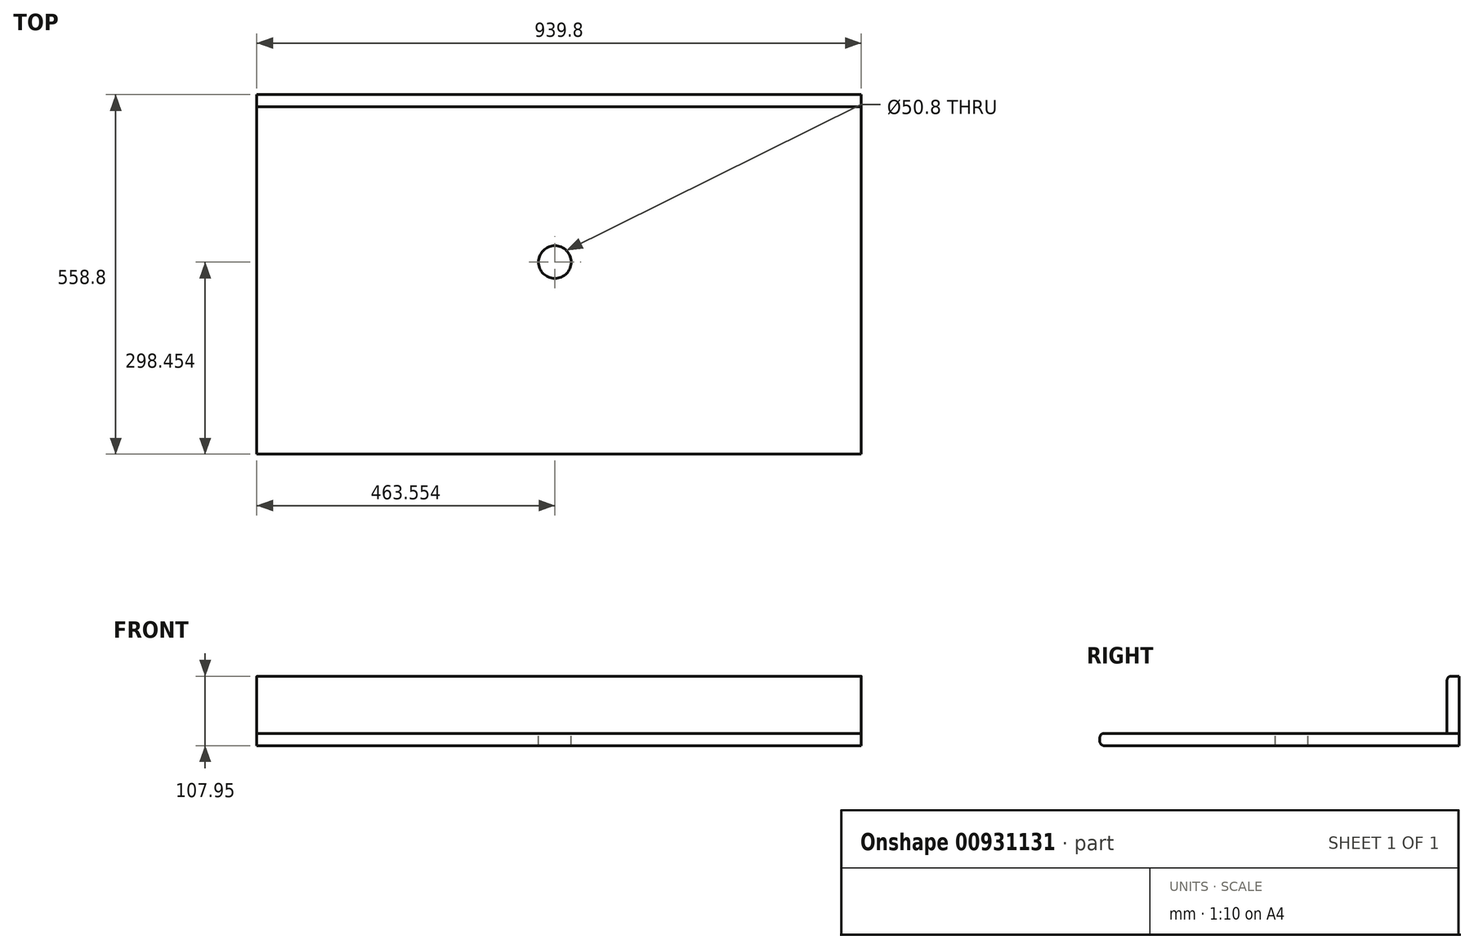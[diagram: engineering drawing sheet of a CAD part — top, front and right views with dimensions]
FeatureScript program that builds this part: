
annotation { "Feature Type Name" : "Feature", "Feature Type Description" : "" }
export const myFeature = defineFeature(function(context is Context, id is Id, definition is map)
    precondition{}
    {
        {
            var Q0;
            Q0=qCreatedBy(makeId("Top.planeOp"),FACE);
            var sketch = newSketch(context, id + "F0", { "sketchPlane" : qUnion([Q0])});
            skLineSegment(sketch, "E0.bottom", {"start": v(-468.4, 352.27) * mm, "end": v(471.4, 352.27) * mm});
            skLineSegment(sketch, "E0.top", {"start": v(-468.4, -206.53) * mm, "end": v(471.4, -206.53) * mm});
            skLineSegment(sketch, "E0.left", {"start": v(-468.4, 352.27) * mm, "end": v(-468.4, -206.53) * mm});
            skLineSegment(sketch, "E0.right", {"start": v(471.4, 352.27) * mm, "end": v(471.4, -206.53) * mm});
            skLineSegment(sketch, "E1.top", {"start": v(-468.4, 333.22) * mm, "end": v(471.4, 333.22) * mm});
            skLineSegment(sketch, "E1.left", {"start": v(-468.4, 352.27) * mm, "end": v(-468.4, 333.22) * mm});
            skLineSegment(sketch, "E1.right", {"start": v(471.4, 352.27) * mm, "end": v(471.4, 333.22) * mm});
            skLineSegment(sketch, "E2", {"start": v(-468.4, 91.92) * mm, "end": v(-4.86, 91.92) * mm});
            skLineSegment(sketch, "E3", {"start": v(-4.86, 91.92) * mm, "end": v(-4.86, -206.53) * mm});
            skCircle(sketch, "E4", {"center": v(-4.86, 91.92) * mm, "radius": 25.4 * mm});
            skSolve(sketch);
        }
        {
            var Q0;
            Q0=makeQuery(id+"F0.imprint","IMPRINT",FACE,{"disambiguationData":[TD([[makeQuery(id+"F0.imprint","IMPRINT",EDGE,{"derivedFrom":sQuery(id+"F0.wireOp",EDGE,"E0.bottom")}),-1.0]])]});
            extrude(context, id + "F1", {"entities" : qUnion([Q0]), "depth" : 88.9 * mm, "offsetDistance" : 25.4 * mm});
        }
        {
            var Q0;
            Q0 = qSketchRegion(id + "F0", true);
            extrude(context, id + "F2", {"entities" : qUnion([Q0]), "depth" : -19.05 * mm, "offsetDistance" : 25.4 * mm});
        }
        {
            var Q0;
            Q0=makeQuery(id+"F1.opExtrude","CAP_EDGE",EDGE,{"disambiguationData":[OSD([sQuery(id+"F0.wireOp",EDGE,"E1.top")])],"isStart":false});
            var Q1;
            Q1=makeQuery(id+"F2.opExtrude","CAP_EDGE",EDGE,{"disambiguationData":[OSD([sQuery(id+"F0.wireOp",EDGE,"E0.top")])],"isStart":true});
            var Q2;
            Q2=makeQuery(id+"F2.opExtrude","CAP_EDGE",EDGE,{"disambiguationData":[OSD([sQuery(id+"F0.wireOp",EDGE,"E0.top")])],"isStart":false});
            fillet(context, id + "F3", {"entities" : qUnion([Q0, Q1, Q2]), "radius" : 6.35 * mm, "tangentPropagation" : true, "allowEdgeOverflow" : false});
        }
    });
